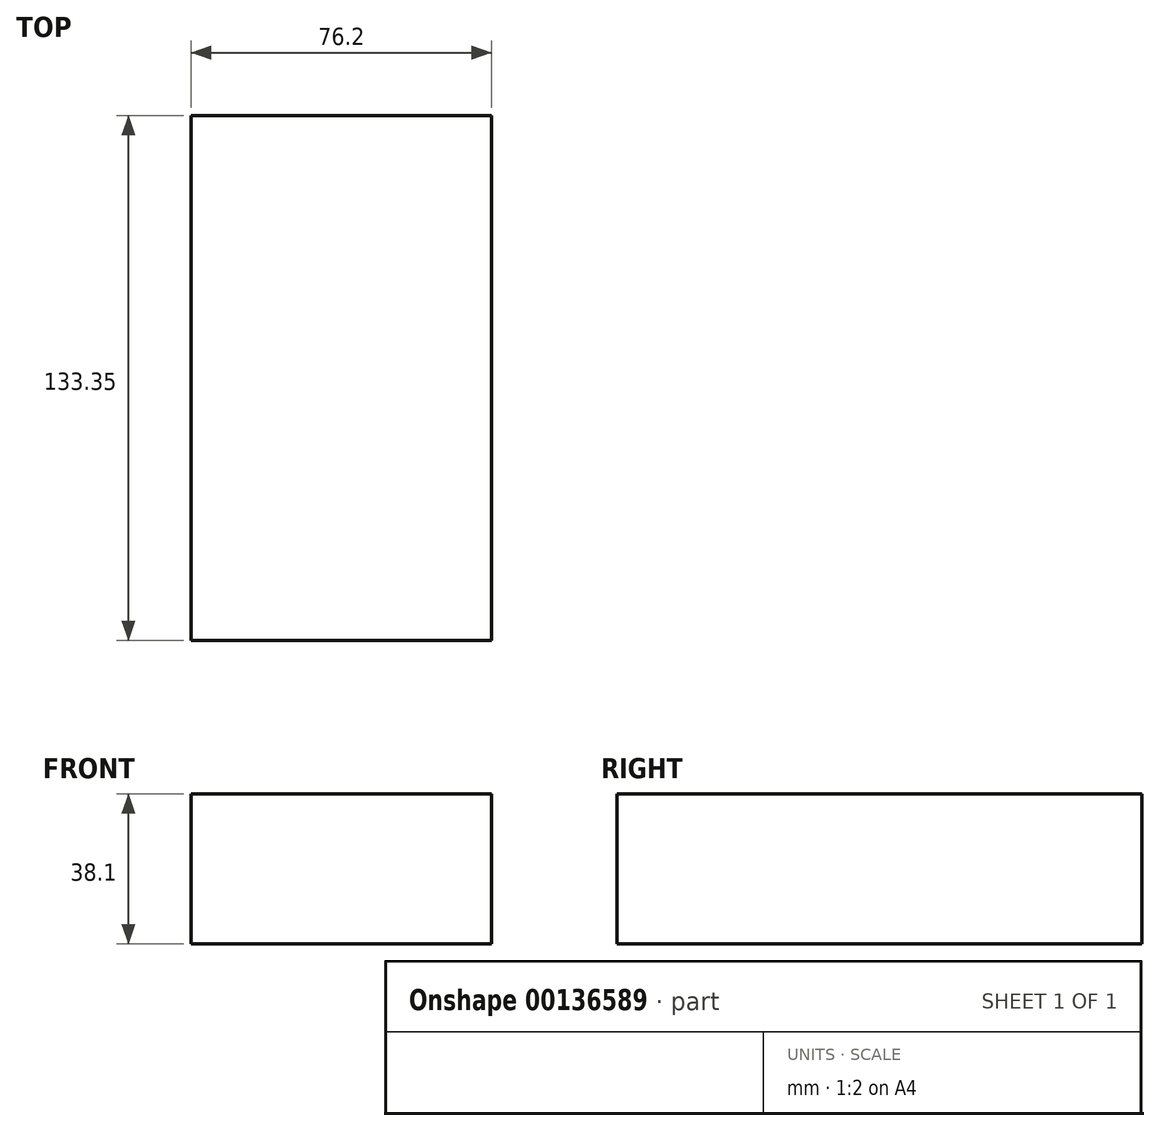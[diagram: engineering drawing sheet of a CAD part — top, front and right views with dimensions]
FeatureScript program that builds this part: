
annotation { "Feature Type Name" : "Feature", "Feature Type Description" : "" }
export const myFeature = defineFeature(function(context is Context, id is Id, definition is map)
    precondition{}
    {
        {
            var Q0;
            Q0=qCreatedBy(makeId("Front.planeOp"),FACE);
            var sketch = newSketch(context, id + "F0", { "sketchPlane" : qUnion([Q0])});
            skLineSegment(sketch, "E0.bottom", {"start": v(0, 0) * mm, "end": v(76.2, 0) * mm});
            skLineSegment(sketch, "E0.top", {"start": v(0, 38.1) * mm, "end": v(76.2, 38.1) * mm});
            skLineSegment(sketch, "E0.left", {"start": v(0, 0) * mm, "end": v(0, 38.1) * mm});
            skLineSegment(sketch, "E0.right", {"start": v(76.2, 0) * mm, "end": v(76.2, 38.1) * mm});
            skSolve(sketch);
        }
        {
            var Q0;
            Q0 = qSketchRegion(id + "F0", true);
            extrude(context, id + "F1", {"entities" : qUnion([Q0]), "depth" : 133.35 * mm});
        }
    });
